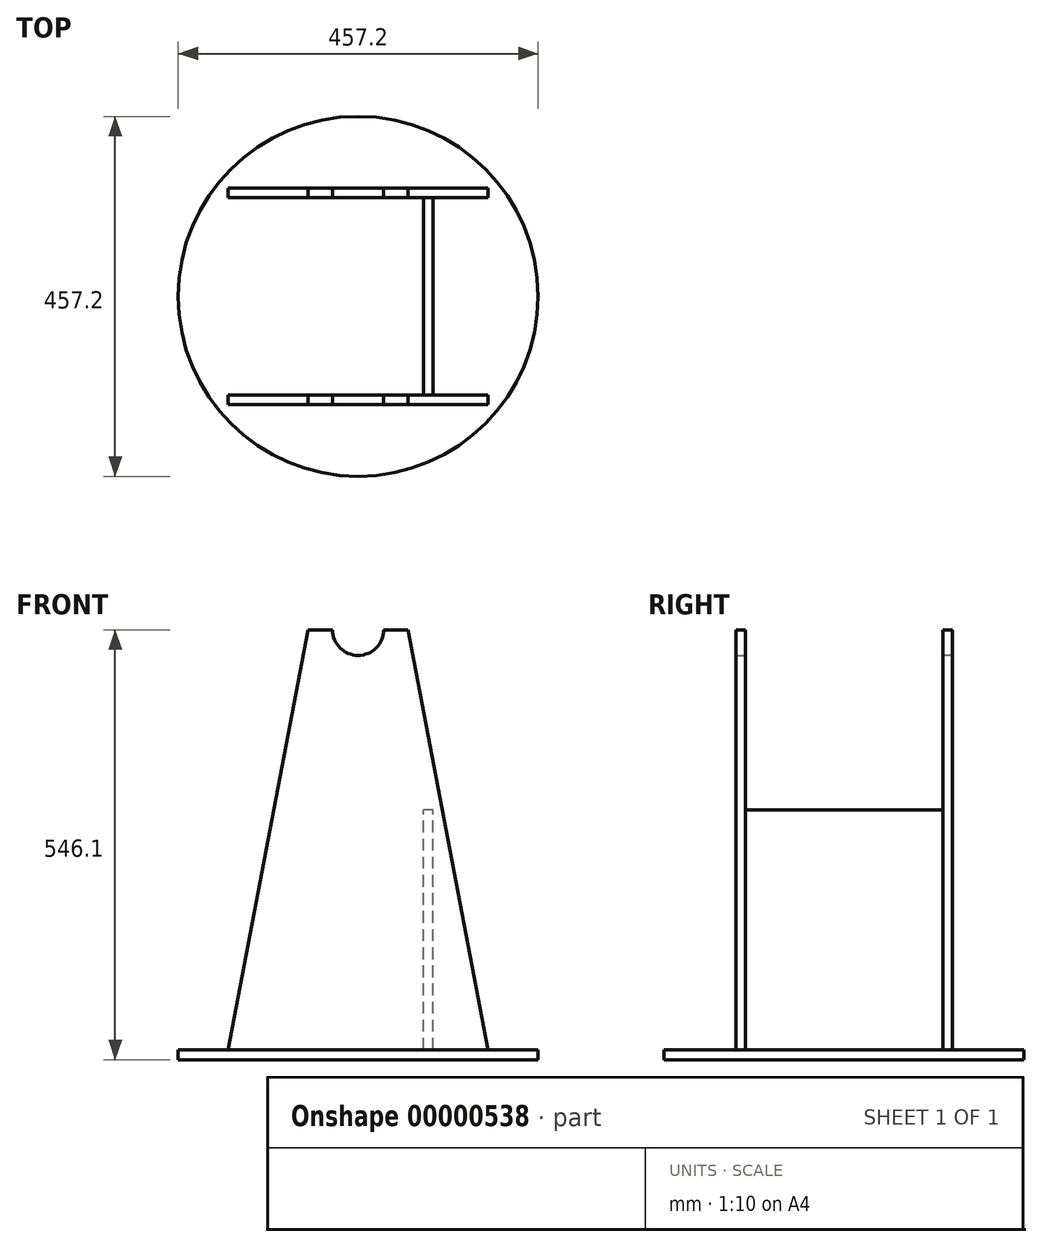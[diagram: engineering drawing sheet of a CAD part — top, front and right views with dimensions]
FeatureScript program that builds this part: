
annotation { "Feature Type Name" : "Feature", "Feature Type Description" : "" }
export const myFeature = defineFeature(function(context is Context, id is Id, definition is map)
    precondition{}
    {
        {
            var Q0;
            Q0=qCreatedBy(makeId("Front.planeOp"),FACE);
            var sketch = newSketch(context, id + "F0", { "sketchPlane" : qUnion([Q0])});
            skLineSegment(sketch, "E0", {"start": v(-165.1, 0) * mm, "end": v(165.1, 0) * mm});
            skLineSegment(sketch, "E1", {"start": v(165.1, 0) * mm, "end": v(63.5, 533.4) * mm});
            skLineSegment(sketch, "E2", {"start": v(63.5, 533.4) * mm, "end": v(-63.5, 533.4) * mm});
            skLineSegment(sketch, "E3", {"start": v(-63.5, 533.4) * mm, "end": v(-165.1, 0) * mm});
            skLineSegment(sketch, "E4", {"start": v(0, 533.4) * mm, "end": v(0, 0) * mm, "construction": true});
            skCircle(sketch, "E5", {"center": v(0, 533.4) * mm, "radius": 32.5 * mm});
            skSolve(sketch);
        }
        {
            var Q0;
            Q0=makeQuery(id+"F0.imprint","IMPRINT",FACE,{"disambiguationData":[TD([[makeQuery(id+"F0.imprint","IMPRINT",EDGE,{"derivedFrom":sQuery(id+"F0.wireOp",EDGE,"E0")}),1.0]])]});
            extrude(context, id + "F1", {"entities" : qUnion([Q0]), "depth" : 12 * mm});
        }
        {
            var Q0;
            Q0=makeQuery(id+"F1.opExtrude","CAP_FACE",FACE,{"disambiguationData":[OSD([sQuery(id+"F0.wireOp",EDGE,"E0"),sQuery(id+"F0.wireOp",EDGE,"E1"),sQuery(id+"F0.wireOp",EDGE,"E2"),sQuery(id+"F0.wireOp",EDGE,"E3"),sQuery(id+"F0.wireOp",EDGE,"E5")])],"isStart":true});
            var sketch = newSketch(context, id + "F2", { "sketchPlane" : qUnion([Q0])});
            skLineSegment(sketch, "E6.bottom", {"start": v(-94.88, 0) * mm, "end": v(-82.88, 0) * mm});
            skLineSegment(sketch, "E6.top", {"start": v(-94.88, 304.8) * mm, "end": v(-82.88, 304.8) * mm});
            skLineSegment(sketch, "E6.left", {"start": v(-94.88, 0) * mm, "end": v(-94.88, 304.8) * mm});
            skLineSegment(sketch, "E6.right", {"start": v(-82.88, 0) * mm, "end": v(-82.88, 304.8) * mm});
            skLineSegment(sketch, "E7", {"start": v(0, 0) * mm, "end": v(0, 310.37) * mm, "construction": true});
            skLineSegment(sketch, "E8.0.MirrorCS", {"start": v(82.88, 0) * mm, "end": v(82.88, 304.8) * mm});
            skLineSegment(sketch, "E9.0.MirrorCS", {"start": v(94.88, 304.8) * mm, "end": v(82.88, 304.8) * mm});
            skLineSegment(sketch, "E10.0.MirrorCS", {"start": v(94.88, 0) * mm, "end": v(94.88, 304.8) * mm});
            skLineSegment(sketch, "E11.0.MirrorCS", {"start": v(94.88, 0) * mm, "end": v(82.88, 0) * mm});
            skSolve(sketch);
        }
        {
            var Q0;
            {Q0=qUnion([makeQuery(id+"F2.imprint","IMPRINT",FACE,{"disambiguationData":[TD([[makeQuery(id+"F2.imprint","IMPRINT",EDGE,{"derivedFrom":sQuery(id+"F2.wireOp",EDGE,"E6.bottom")}),-1.0]])]}),makeQuery(id+"F2.imprint","IMPRINT",FACE,{"disambiguationData":[TD([[makeQuery(id+"F2.imprint","IMPRINT",EDGE,{"derivedFrom":sQuery(id+"F2.wireOp",EDGE,"E8.0.MirrorCS")}),-1.0]])]})]);}
            extrude(context, id + "F3", {"entities" : qUnion([Q0]), "depth" : 250.82 * mm});
        }
        {
            var Q0;
            Q0=makeQuery(id+"F3.opExtrude","CAP_FACE",FACE,{"disambiguationData":[OSD([sQuery(id+"F2.wireOp",EDGE,"E8.0.MirrorCS"),sQuery(id+"F2.wireOp",EDGE,"E9.0.MirrorCS"),sQuery(id+"F2.wireOp",EDGE,"E10.0.MirrorCS"),sQuery(id+"F2.wireOp",EDGE,"E11.0.MirrorCS")])],"isStart":true});
            var Q1;
            Q1=makeQuery(id+"F3.opExtrude","CAP_FACE",FACE,{"disambiguationData":[OSD([sQuery(id+"F2.wireOp",EDGE,"E8.0.MirrorCS"),sQuery(id+"F2.wireOp",EDGE,"E9.0.MirrorCS"),sQuery(id+"F2.wireOp",EDGE,"E10.0.MirrorCS"),sQuery(id+"F2.wireOp",EDGE,"E11.0.MirrorCS")])],"isStart":false});
            cPlane(context, id + "F4", {"entities" : qUnion([Q0, Q1]), "cplaneType" : CPlaneType.MID_PLANE, "offset" : 150 * mm, "width" : 150 * mm, "height" : 150 * mm});
        }
        {
            var Q0;
            Q0=makeQuery(id+"F1.opExtrude","SWEPT_BODY",BODY,{"disambiguationData":[OSD([sQuery(id+"F0.wireOp",EDGE,"E0"),sQuery(id+"F0.wireOp",EDGE,"E1"),sQuery(id+"F0.wireOp",EDGE,"E2"),sQuery(id+"F0.wireOp",EDGE,"E3"),sQuery(id+"F0.wireOp",EDGE,"E5")])]});
            var Q1;
            Q1=qCreatedBy(id+"F4.planeOp",FACE);
            mirror(context, id + "F5", {"entities" : qUnion([Q0]), "mirrorPlane" : qUnion([Q1])});
        }
        {
            var Q0;
            Q0=qCreatedBy(makeId("Top.planeOp"),FACE);
            var sketch = newSketch(context, id + "F6", { "sketchPlane" : qUnion([Q0])});
            skLineSegment(sketch, "E12", {"start": v(-82.88, 250.83) * mm, "end": v(82.88, 0) * mm, "construction": true});
            skCircle(sketch, "E13", {"center": v(0, 125.41) * mm, "radius": 228.6 * mm});
            skSolve(sketch);
        }
        {
            var Q0;
            Q0=makeQuery(id+"F6.imprint","IMPRINT",FACE,{"disambiguationData":[TD([[makeQuery(id+"F6.imprint","IMPRINT",EDGE,{"derivedFrom":sQuery(id+"F6.wireOp",EDGE,"E13")}),1.0]])]});
            extrude(context, id + "F7", {"entities" : qUnion([Q0]), "oppositeDirection" : true, "depth" : 12.7 * mm});
        }
        {
            var Q0;
            Q0=makeQuery(id+"F3.opExtrude","SWEPT_BODY",BODY,{"disambiguationData":[OSD([sQuery(id+"F2.wireOp",EDGE,"E8.0.MirrorCS"),sQuery(id+"F2.wireOp",EDGE,"E9.0.MirrorCS"),sQuery(id+"F2.wireOp",EDGE,"E10.0.MirrorCS"),sQuery(id+"F2.wireOp",EDGE,"E11.0.MirrorCS")])]});
            deleteBodies(context, id + "F8", {"entities" : qUnion([Q0])});
        }
    });
